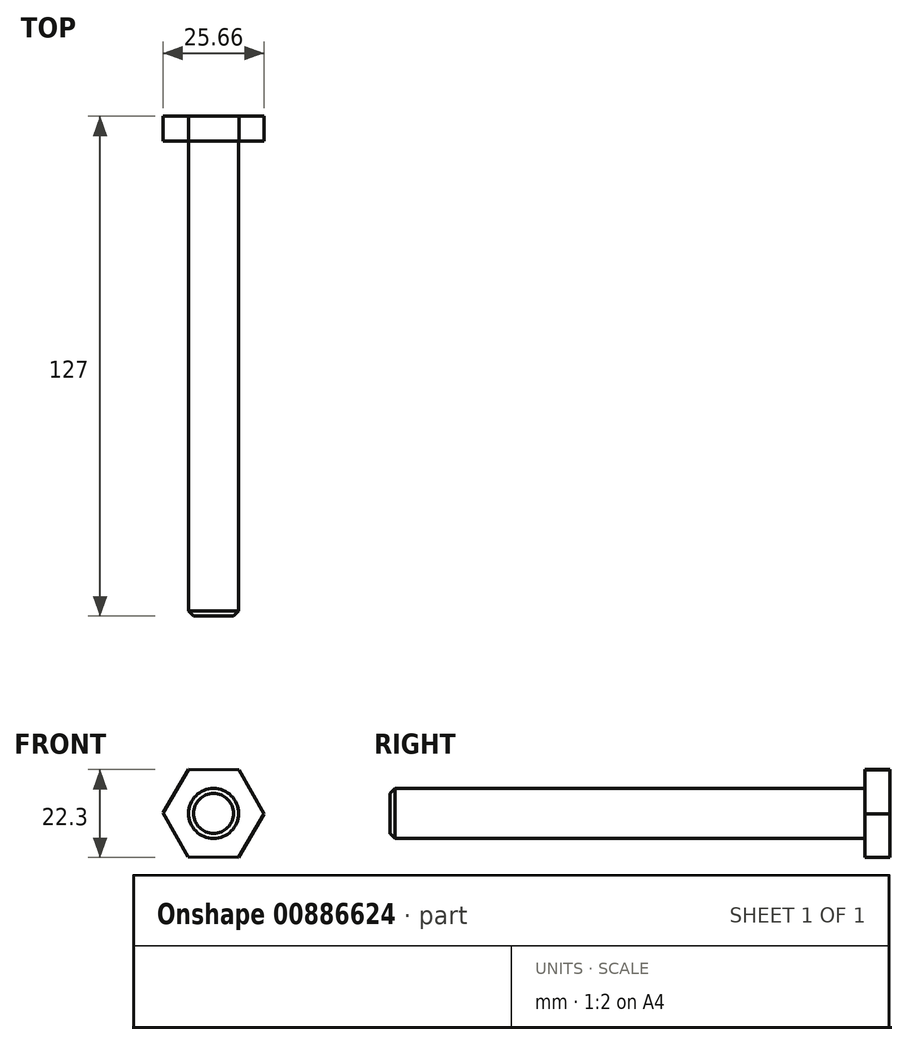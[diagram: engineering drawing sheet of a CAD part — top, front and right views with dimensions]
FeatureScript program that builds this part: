
annotation { "Feature Type Name" : "Feature", "Feature Type Description" : "" }
export const myFeature = defineFeature(function(context is Context, id is Id, definition is map)
    precondition{}
    {
        {
            var Q0;
            Q0=qCreatedBy(makeId("Front.planeOp"),FACE);
            var sketch = newSketch(context, id + "F0", { "sketchPlane" : qUnion([Q0])});
            skCircle(sketch, "E0.cCircle", {"center": v(0, 0) * mm, "radius": 11.11 * mm, "construction": true});
            skLineSegment(sketch, "E0.0", {"start": v(12.83, -0.07) * mm, "end": v(6.35, -11.15) * mm});
            skLineSegment(sketch, "E0.1", {"start": v(6.35, -11.15) * mm, "end": v(-6.48, -11.08) * mm});
            skLineSegment(sketch, "E0.2", {"start": v(-6.48, -11.08) * mm, "end": v(-12.83, 0.07) * mm});
            skLineSegment(sketch, "E0.3", {"start": v(-12.83, 0.07) * mm, "end": v(-6.35, 11.15) * mm});
            skLineSegment(sketch, "E0.4", {"start": v(-6.35, 11.15) * mm, "end": v(6.48, 11.08) * mm});
            skLineSegment(sketch, "E0.5", {"start": v(6.48, 11.08) * mm, "end": v(12.83, -0.07) * mm});
            skPoint(sketch, "E0.0.midPoint", {"position": v(9.6, -5.61) * mm});
            skSolve(sketch);
        }
        {
            var Q0;
            Q0=makeQuery(id+"F0.imprint","IMPRINT",FACE,{"disambiguationData":[TD([[makeQuery(id+"F0.imprint","IMPRINT",EDGE,{"derivedFrom":sQuery(id+"F0.wireOp",EDGE,"E0.0")}),-1.0]])]});
            extrude(context, id + "F1", {"entities" : qUnion([Q0]), "depth" : 6.35 * mm, "offsetDistance" : 25.4 * mm});
        }
        {
            var Q0;
            Q0=qCreatedBy(makeId("Front.planeOp"),FACE);
            var sketch = newSketch(context, id + "F2", { "sketchPlane" : qUnion([Q0])});
            skCircle(sketch, "E1", {"center": v(0, 0) * mm, "radius": 6.35 * mm});
            skSolve(sketch);
        }
        {
            var Q0;
            Q0=makeQuery(id+"F2.imprint","IMPRINT",FACE,{"disambiguationData":[TD([[makeQuery(id+"F2.imprint","IMPRINT",EDGE,{"derivedFrom":sQuery(id+"F2.wireOp",EDGE,"E1")}),1.0]])]});
            extrude(context, id + "F3", {"entities" : qUnion([Q0]), "operationType" : NewBodyOperationType.ADD, "depth" : 127 * mm, "offsetDistance" : 25.4 * mm});
        }
        {
            var Q0;
            Q0=makeQuery(id+"F3.opExtrude","CAP_EDGE",EDGE,{"disambiguationData":[OSD([sQuery(id+"F2.wireOp",EDGE,"E1")])],"isStart":false});
            chamfer(context, id + "F4", {"entities" : qUnion([Q0]), "width" : 1.27 * mm, "tangentPropagation" : true});
        }
    });
